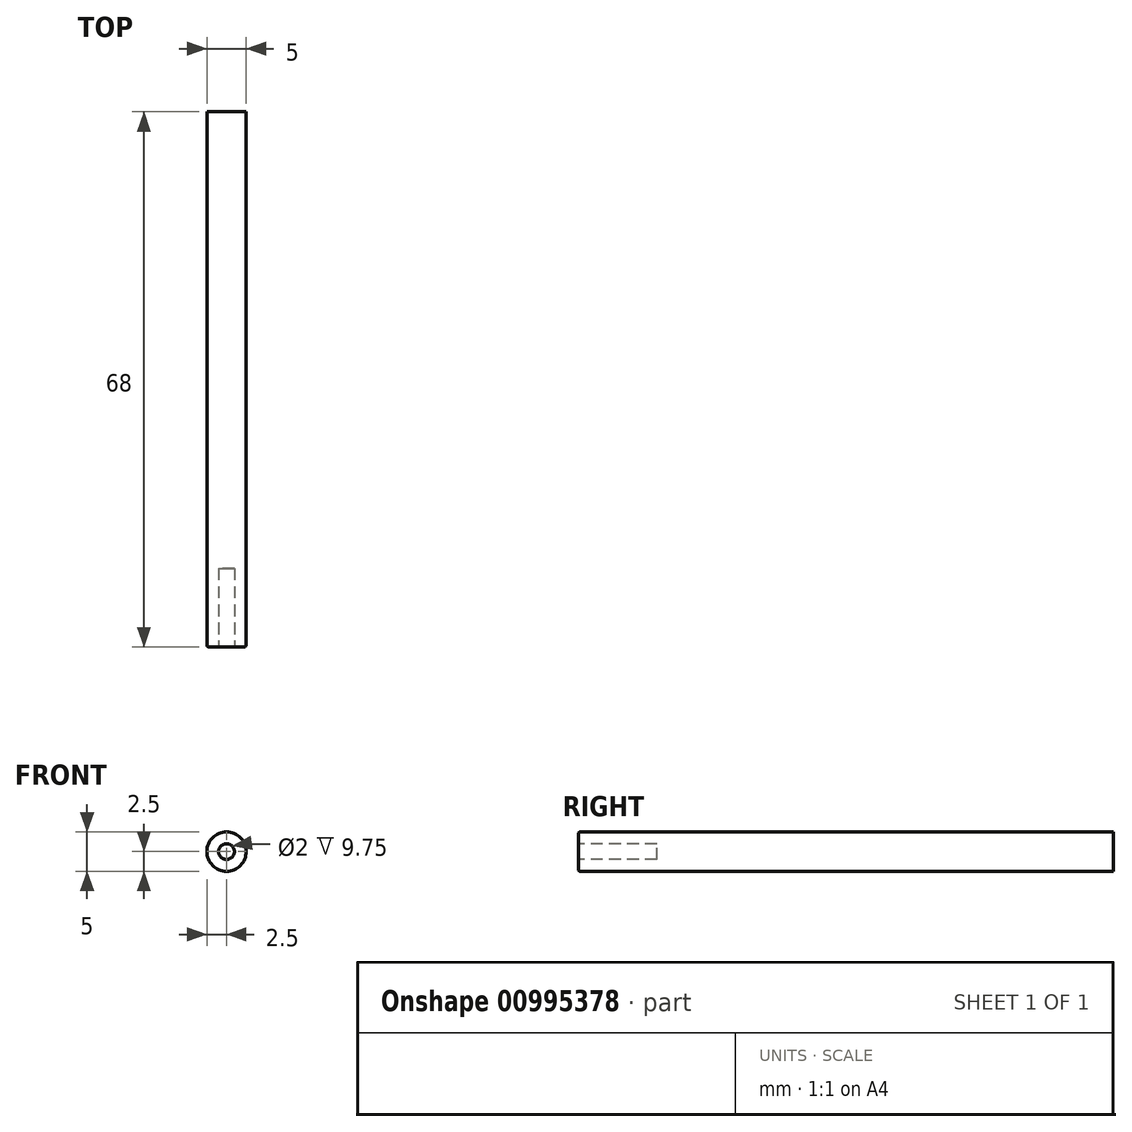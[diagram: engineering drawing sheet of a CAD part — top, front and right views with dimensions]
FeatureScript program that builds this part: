
annotation { "Feature Type Name" : "Feature", "Feature Type Description" : "" }
export const myFeature = defineFeature(function(context is Context, id is Id, definition is map)
    precondition{}
    {
        {
            var Q0;
            Q0=qCreatedBy(makeId("Front.planeOp"),FACE);
            var sketch = newSketch(context, id + "F0", { "sketchPlane" : qUnion([Q0])});
            skCircle(sketch, "E0", {"center": v(0, 0) * mm, "radius": 2.5 * mm});
            skSolve(sketch);
        }
        {
            var Q0;
            Q0 = qSketchRegion(id + "F0", true);
            extrude(context, id + "F1", {"entities" : qUnion([Q0]), "depth" : 68 * mm, "offsetDistance" : 25 * mm});
        }
        {
            var Q0;
            Q0=makeQuery(id+"F1.opExtrude","CAP_FACE",FACE,{"disambiguationData":[OSD([sQuery(id+"F0.wireOp",EDGE,"E0")])],"isStart":false});
            var sketch = newSketch(context, id + "F2", { "sketchPlane" : qUnion([Q0])});
            skCircle(sketch, "E1", {"center": v(0, 0) * mm, "radius": 1 * mm});
            skSolve(sketch);
        }
        {
            var Q0;
            Q0 = qSketchRegion(id + "F2", true);
            extrude(context, id + "F3", {"entities" : qUnion([Q0]), "operationType" : NewBodyOperationType.REMOVE, "oppositeDirection" : true, "depth" : 10 * mm, "offsetDistance" : 25 * mm});
        }
        {
            var Q0;
            Q0=makeQuery(id+"F1.opExtrude","CAP_FACE",FACE,{"disambiguationData":[OSD([sQuery(id+"F0.wireOp",EDGE,"E0")])],"isStart":false});
            fillet(context, id + "F4", {"entities" : qUnion([Q0]), "radius" : .25 * mm, "tangentPropagation" : true, "allowEdgeOverflow" : false});
        }
    });
